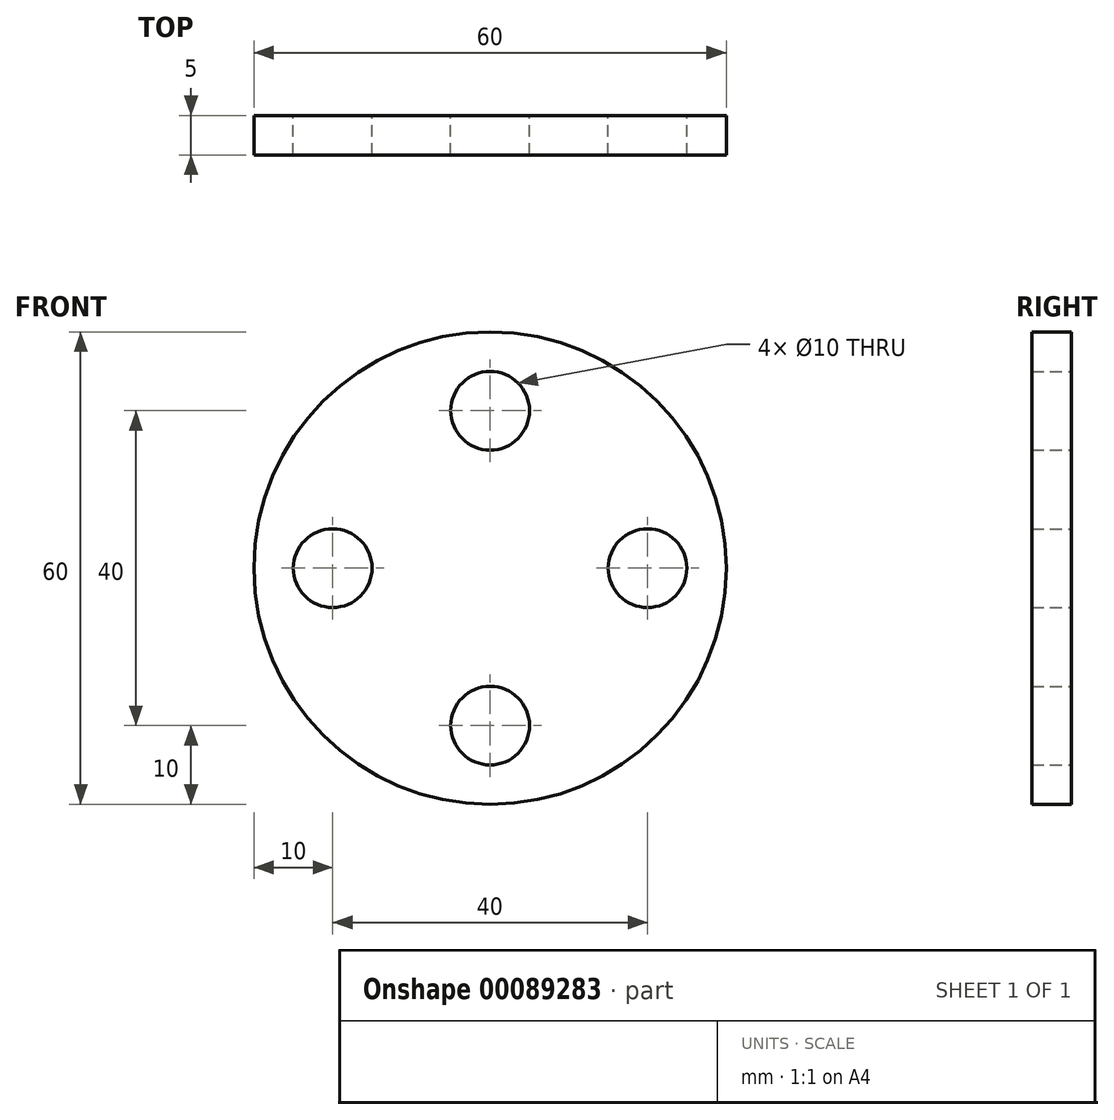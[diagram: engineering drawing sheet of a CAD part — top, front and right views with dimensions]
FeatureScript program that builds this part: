
annotation { "Feature Type Name" : "Feature", "Feature Type Description" : "" }
export const myFeature = defineFeature(function(context is Context, id is Id, definition is map)
    precondition{}
    {
        {
            var Q0;
            Q0=qCreatedBy(makeId("Front.planeOp"),FACE);
            var sketch = newSketch(context, id + "F0", { "sketchPlane" : qUnion([Q0])});
            skCircle(sketch, "E0", {"center": v(0, 0) * mm, "radius": 30 * mm});
            skCircle(sketch, "E1", {"center": v(0, 0) * mm, "radius": 20 * mm, "construction": true});
            skLineSegment(sketch, "E2", {"start": v(-30, 0) * mm, "end": v(30, 0) * mm, "construction": true});
            skLineSegment(sketch, "E3", {"start": v(0, 30) * mm, "end": v(0, -30) * mm, "construction": true});
            skCircle(sketch, "E4", {"center": v(0, 20) * mm, "radius": 5 * mm});
            skCircle(sketch, "E5", {"center": v(-20, 0) * mm, "radius": 5 * mm});
            skCircle(sketch, "E6", {"center": v(20, 0) * mm, "radius": 5 * mm});
            skCircle(sketch, "E7", {"center": v(0, -20) * mm, "radius": 5 * mm});
            skSolve(sketch);
        }
        {
            var Q0;
            Q0 = qSketchRegion(id + "F0", true);
            extrude(context, id + "F1", {"entities" : qUnion([Q0]), "depth" : 5 * mm});
        }
    });
